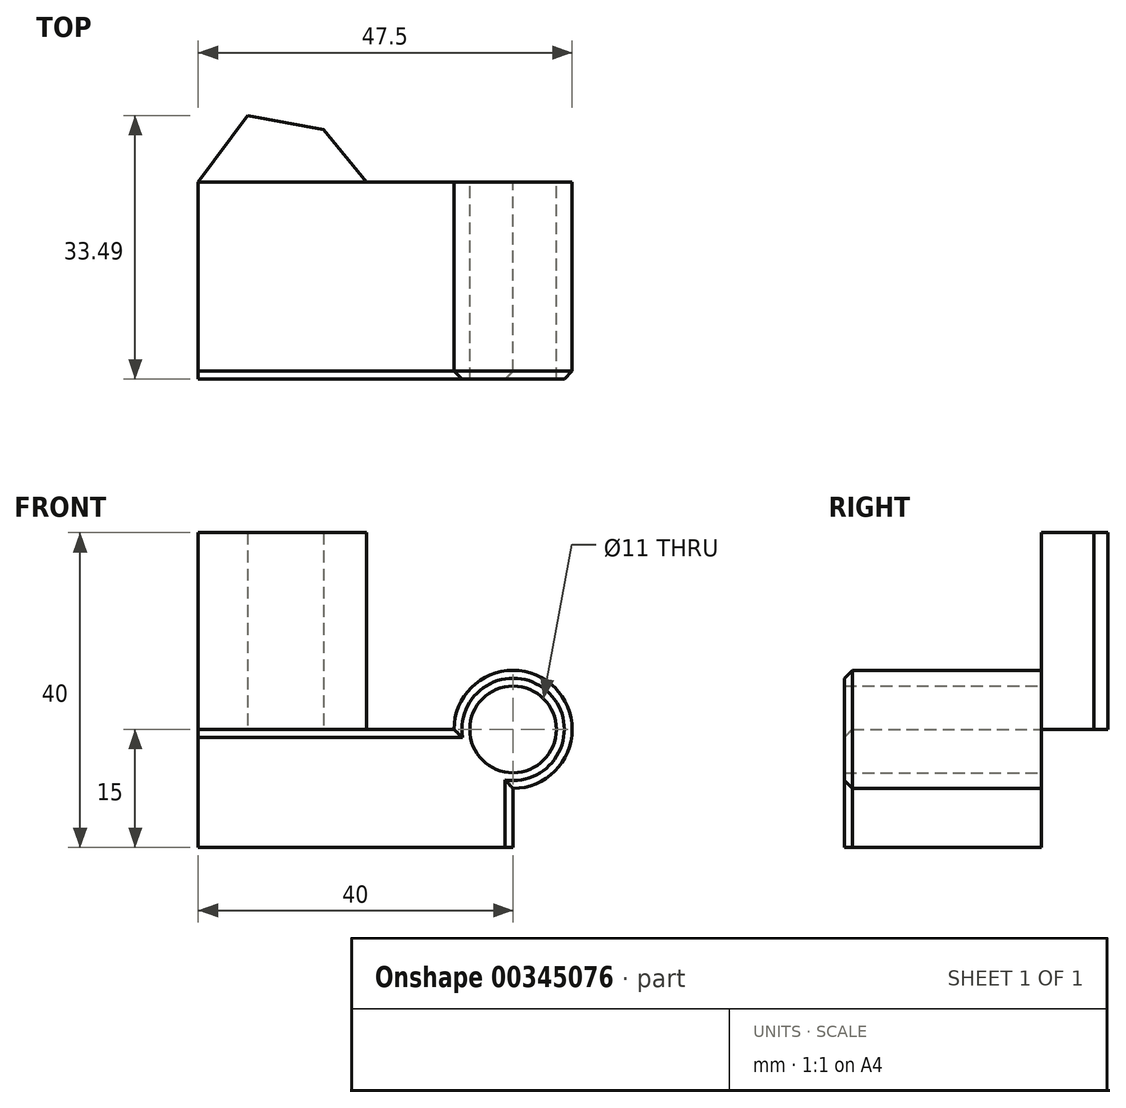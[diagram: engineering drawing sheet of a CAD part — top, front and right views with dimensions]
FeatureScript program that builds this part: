
annotation { "Feature Type Name" : "Feature", "Feature Type Description" : "" }
export const myFeature = defineFeature(function(context is Context, id is Id, definition is map)
    precondition{}
    {
        {
            var Q0;
            Q0=qCreatedBy(makeId("Front.planeOp"),FACE);
            var sketch = newSketch(context, id + "F0", { "sketchPlane" : qUnion([Q0])});
            skLineSegment(sketch, "E0.bottom", {"start": v(0, 0) * mm, "end": v(40, 0) * mm});
            skLineSegment(sketch, "E0.top", {"start": v(0, 15) * mm, "end": v(40, 15) * mm});
            skLineSegment(sketch, "E0.left", {"start": v(0, 0) * mm, "end": v(0, 15) * mm});
            skLineSegment(sketch, "E0.right", {"start": v(40, 0) * mm, "end": v(40, 15) * mm});
            skCircle(sketch, "E1", {"center": v(40, 15) * mm, "radius": 7.5 * mm});
            skSolve(sketch);
        }
        {
            var Q0;
            {var subQ1=sQuery(id+"F0.wireOp",EDGE,"E0.bottom");Q0=makeQuery(id+"F0.imprint","IMPRINT",FACE,{"disambiguationData":[TD([[makeQuery(id+"F0.imprint","IMPRINT",EDGE,{"derivedFrom":subQ1}),1.0]])]});}
            var Q1;
            {var subQ0=sQuery(id+"F0.wireOp",EDGE,"E0.right");var subQ1=sQuery(id+"F0.wireOp",EDGE,"E0.top");var subQ2=makeQuery(id+"F0.imprint","INTERSECT",VERTEX,{"derivedFrom":[subQ1,subQ0]});Q1=makeQuery(id+"F0.imprint","IMPRINT",FACE,{"disambiguationData":[TD([[makeQuery(id+"F0.imprint","IMPRINT",EDGE,{"disambiguationData":[TD([[subQ2,1.0]])],"derivedFrom":subQ1}),-1.0]])]});}
            var Q2;
            {var subQ0=sQuery(id+"F0.wireOp",EDGE,"E0.right");var subQ1=sQuery(id+"F0.wireOp",EDGE,"E0.top");var subQ2=makeQuery(id+"F0.imprint","INTERSECT",VERTEX,{"derivedFrom":[subQ1,subQ0]});Q2=makeQuery(id+"F0.imprint","IMPRINT",FACE,{"disambiguationData":[TD([[makeQuery(id+"F0.imprint","IMPRINT",EDGE,{"disambiguationData":[TD([[subQ2,1.0]])],"derivedFrom":subQ1}),1.0]])]});}
            extrude(context, id + "F1", {"entities" : qUnion([Q0, Q1, Q2]), "depth" : 25 * mm});
        }
        {
            var Q0;
            Q0=makeQuery(id+"F1.opExtrude","CAP_EDGE",EDGE,{"disambiguationData":[OSD([sQuery(id+"F0.wireOp",EDGE,"E0.top")])],"isStart":false});
            var Q1;
            Q1=makeQuery(id+"F1.opExtrude","CAP_EDGE",EDGE,{"disambiguationData":[OSD([sQuery(id+"F0.wireOp",EDGE,"E1")])],"isStart":false});
            var Q2;
            Q2=makeQuery(id+"F1.opExtrude","CAP_EDGE",EDGE,{"disambiguationData":[OSD([sQuery(id+"F0.wireOp",EDGE,"E0.right")])],"isStart":false});
            chamfer(context, id + "F2", {"entities" : qUnion([Q0, Q1, Q2]), "width" : 1 * mm, "tangentPropagation" : true});
        }
        {
            var Q0;
            Q0=makeQuery(id+"F1.opExtrude","CAP_FACE",FACE,{"disambiguationData":[OSD([sQuery(id+"F0.wireOp",EDGE,"E0.bottom"),sQuery(id+"F0.wireOp",EDGE,"E0.top"),sQuery(id+"F0.wireOp",EDGE,"E0.left"),sQuery(id+"F0.wireOp",EDGE,"E0.right"),sQuery(id+"F0.wireOp",EDGE,"E1")])],"isStart":true});
            var sketch = newSketch(context, id + "F3", { "sketchPlane" : qUnion([Q0])});
            skArc(sketch, "E2.0", {"start": v(-40, 7.5) * mm, "mid": v(-45.3, 20.3) * mm, "end": v(-32.5, 15) * mm});
            skCircle(sketch, "E3", {"center": v(-40, 15) * mm, "radius": 5.5 * mm});
            skSolve(sketch);
        }
        {
            var Q0;
            Q0=makeQuery(id+"F3.imprint","IMPRINT",FACE,{"disambiguationData":[TD([[makeQuery(id+"F3.imprint","IMPRINT",EDGE,{"derivedFrom":sQuery(id+"F3.wireOp",EDGE,"E3")}),1.0]])]});
            extrude(context, id + "F4", {"entities" : qUnion([Q0]), "operationType" : NewBodyOperationType.REMOVE, "endBound" : BoundingType.THROUGH_ALL, "oppositeDirection" : true, "depth" : 25 * mm});
        }
        {
            var Q0;
            Q0=makeQuery(id+"F1.opExtrude","SWEPT_FACE",FACE,{"disambiguationData":[OSD([sQuery(id+"F0.wireOp",EDGE,"E0.top")])]});
            var sketch = newSketch(context, id + "F5", { "sketchPlane" : qUnion([Q0])});
            skLineSegment(sketch, "E4", {"start": v(0, 0) * mm, "end": v(6.26, 8.49) * mm});
            skLineSegment(sketch, "E5", {"start": v(6.26, 8.49) * mm, "end": v(15.9, 6.72) * mm});
            skLineSegment(sketch, "E6", {"start": v(15.9, 6.72) * mm, "end": v(21.36, 0) * mm});
            skSolve(sketch);
        }
        {
            var Q0;
            {var subQ0=sQuery(id+"F5.wireOp",EDGE,"E4");Q0=makeQuery(id+"F5.imprint","IMPRINT",FACE,{"disambiguationData":[TD([[makeQuery(id+"F5.imprint","IMPRINT",EDGE,{"derivedFrom":subQ0}),-1.0]])]});}
            extrude(context, id + "F6", {"entities" : qUnion([Q0]), "depth" : 25 * mm});
        }
    });
